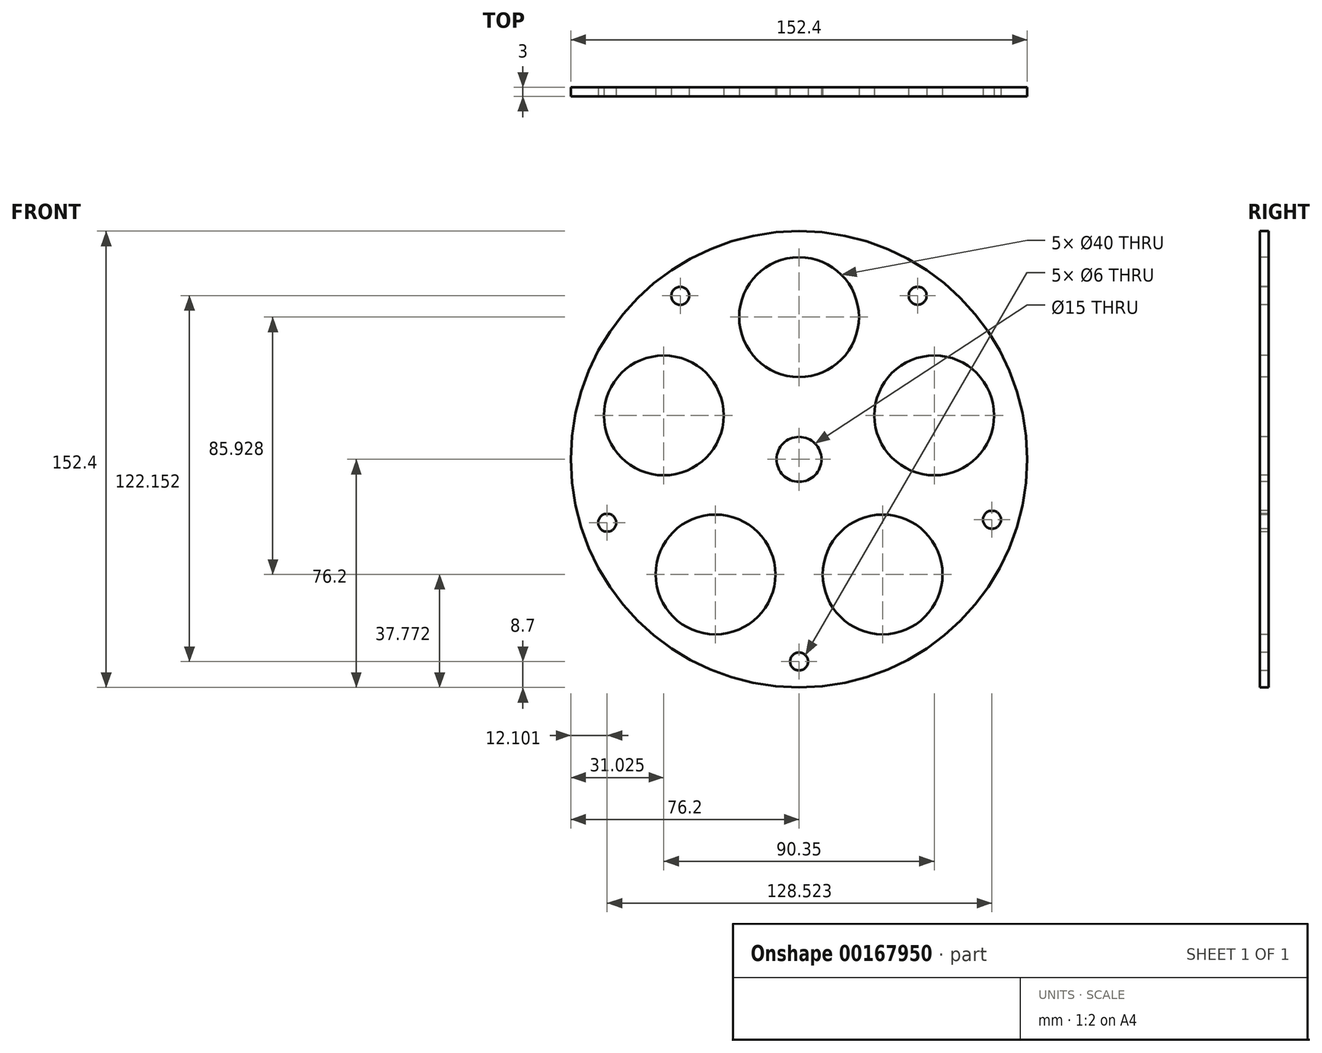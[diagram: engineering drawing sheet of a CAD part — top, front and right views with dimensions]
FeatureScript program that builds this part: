
annotation { "Feature Type Name" : "Feature", "Feature Type Description" : "" }
export const myFeature = defineFeature(function(context is Context, id is Id, definition is map)
    precondition{}
    {
        {
            var Q0;
            Q0=qCreatedBy(makeId("Front.planeOp"),FACE);
            var sketch = newSketch(context, id + "F0", { "sketchPlane" : qUnion([Q0])});
            skCircle(sketch, "E0", {"center": v(0, 0) * mm, "radius": 76.2 * mm});
            skLineSegment(sketch, "E1", {"start": v(-126.87, 0) * mm, "end": v(76.2, 0) * mm, "construction": true});
            skLineSegment(sketch, "E2", {"start": v(0, 129.98) * mm, "end": v(0, -100.88) * mm, "construction": true});
            skLineSegment(sketch, "E3", {"start": v(0, 0) * mm, "end": v(136.58, 44.38) * mm, "construction": true});
            skLineSegment(sketch, "E4", {"start": v(0, 0) * mm, "end": v(-120.7, 39.21) * mm, "construction": true});
            skLineSegment(sketch, "E5", {"start": v(0, 0) * mm, "end": v(-76.95, -105.9) * mm, "construction": true});
            skLineSegment(sketch, "E6", {"start": v(0, 0) * mm, "end": v(78.85, -108.53) * mm, "construction": true});
            skCircle(sketch, "E7", {"center": v(0, 0) * mm, "radius": 47.5 * mm, "construction": true});
            skCircle(sketch, "E8", {"center": v(-45.18, 14.68) * mm, "radius": 25 * mm, "construction": true});
            skCircle(sketch, "E9", {"center": v(45.18, 14.68) * mm, "radius": 25 * mm, "construction": true});
            skCircle(sketch, "E10", {"center": v(0, 47.5) * mm, "radius": 25 * mm, "construction": true});
            skCircle(sketch, "E11", {"center": v(-27.92, -38.43) * mm, "radius": 25 * mm, "construction": true});
            skCircle(sketch, "E12", {"center": v(27.92, -38.43) * mm, "radius": 25 * mm, "construction": true});
            skLineSegment(sketch, "E13", {"start": v(0, 0) * mm, "end": v(-69.91, 96.23) * mm, "construction": true});
            skLineSegment(sketch, "E14", {"start": v(0, 0) * mm, "end": v(-111.32, -36.74) * mm, "construction": true});
            skLineSegment(sketch, "E15", {"start": v(0, 0) * mm, "end": v(0, -109.6) * mm, "construction": true});
            skLineSegment(sketch, "E16", {"start": v(0, 0) * mm, "end": v(108.9, -34.05) * mm, "construction": true});
            skLineSegment(sketch, "E17", {"start": v(0, 0) * mm, "end": v(68.5, 94.5) * mm, "construction": true});
            skCircle(sketch, "E18", {"center": v(-39.68, 54.6) * mm, "radius": 12.7 * mm, "construction": true});
            skCircle(sketch, "E19", {"center": v(0, 0) * mm, "radius": 67.5 * mm, "construction": true});
            skCircle(sketch, "E20", {"center": v(-64.1, -21.16) * mm, "radius": 12.7 * mm, "construction": true});
            skCircle(sketch, "E21", {"center": v(0, -67.5) * mm, "radius": 12.7 * mm, "construction": true});
            skCircle(sketch, "E22", {"center": v(64.42, -20.14) * mm, "radius": 12.7 * mm, "construction": true});
            skCircle(sketch, "E23", {"center": v(39.62, 54.65) * mm, "radius": 12.7 * mm, "construction": true});
            skCircle(sketch, "E24", {"center": v(0, 0) * mm, "radius": 7.5 * mm});
            skSolve(sketch);
        }
        {
            var Q0;
            Q0=qCreatedBy(makeId("Front.planeOp"),FACE);
            var sketch = newSketch(context, id + "F1", { "sketchPlane" : qUnion([Q0])});
            skCircle(sketch, "E25.0", {"center": v(0, 0) * mm, "radius": 76.2 * mm});
            skCircle(sketch, "E26.0", {"center": v(0, 0) * mm, "radius": 7.5 * mm});
            skCircle(sketch, "E27", {"center": v(0, 47.5) * mm, "radius": 20 * mm});
            skCircle(sketch, "E28", {"center": v(-45.18, 14.68) * mm, "radius": 20 * mm});
            skCircle(sketch, "E29", {"center": v(-27.92, -38.43) * mm, "radius": 20 * mm});
            skCircle(sketch, "E30", {"center": v(27.92, -38.43) * mm, "radius": 20 * mm});
            skCircle(sketch, "E31", {"center": v(45.18, 14.68) * mm, "radius": 20 * mm});
            skCircle(sketch, "E32", {"center": v(-39.68, 54.6) * mm, "radius": 3 * mm});
            skCircle(sketch, "E33", {"center": v(-64.1, -21.16) * mm, "radius": 3 * mm});
            skCircle(sketch, "E34", {"center": v(0, -67.5) * mm, "radius": 3 * mm});
            skCircle(sketch, "E35", {"center": v(64.42, -20.14) * mm, "radius": 3 * mm});
            skCircle(sketch, "E36", {"center": v(39.62, 54.65) * mm, "radius": 3 * mm});
            skSolve(sketch);
        }
        {
            var Q0;
            Q0 = qSketchRegion(id + "F1", true);
            extrude(context, id + "F2", {"entities" : qUnion([Q0]), "oppositeDirection" : true, "depth" : 3 * mm});
        }
    });
